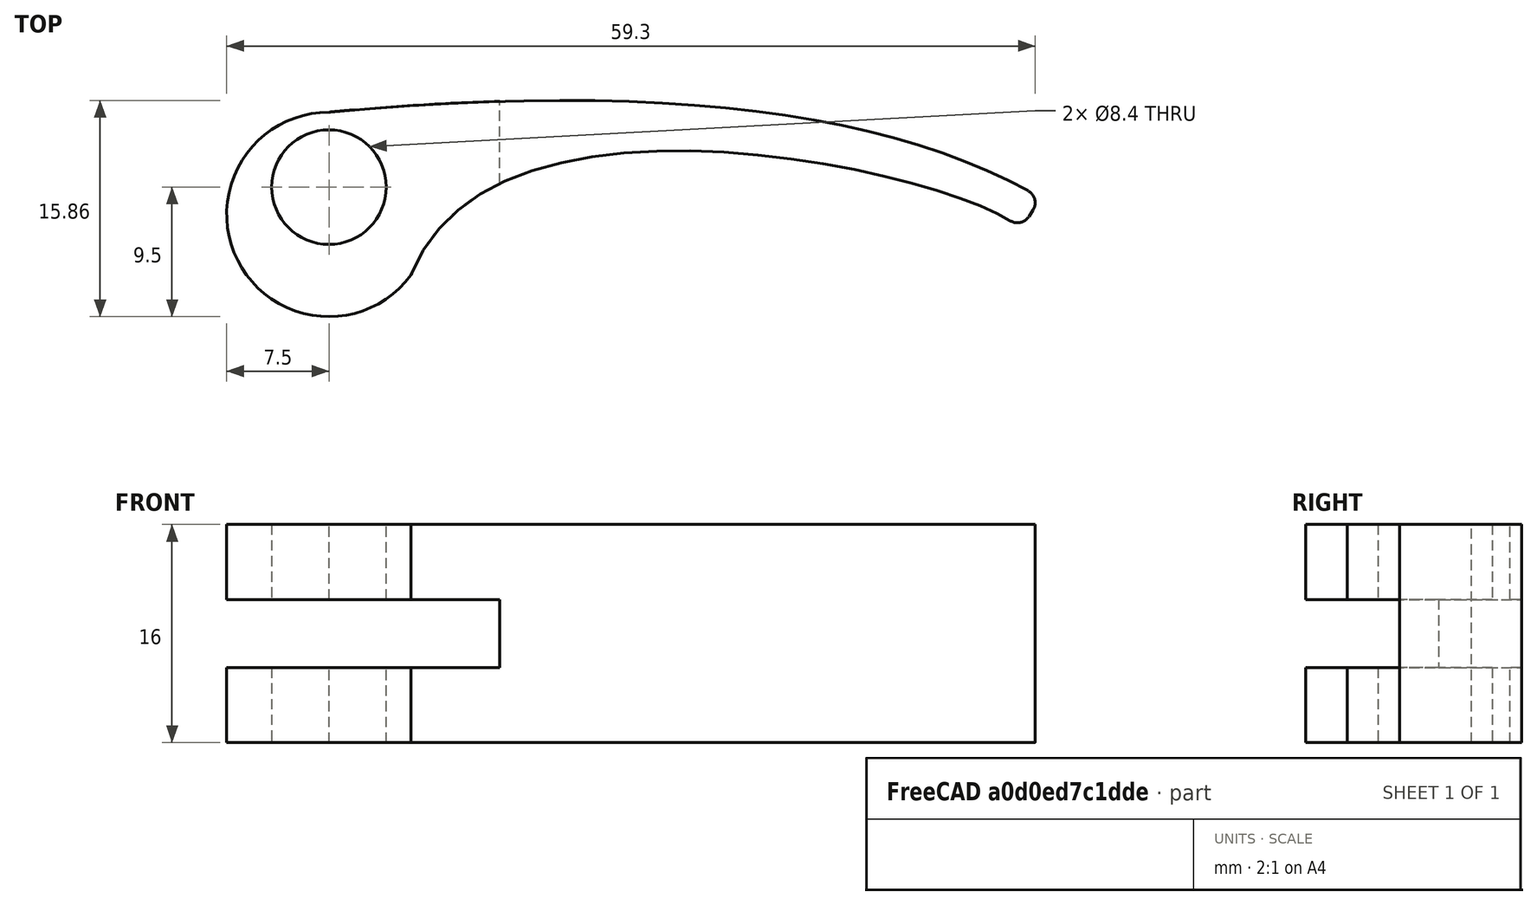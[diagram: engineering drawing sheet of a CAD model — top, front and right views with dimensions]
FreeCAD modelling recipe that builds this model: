
FCSTD DOCUMENT  (FreeCAD 0.18R16131 (Git))
Label: quick_release_handle
License: All rights reserved
LicenseURL: http://en.wikipedia.org/wiki/All_rights_reserved
objects: Sketcher::SketchObject×2, PartDesign::Pad×1, PartDesign::Fillet×1, PartDesign::Pocket×1, PartDesign::Body×1
note: 8 computed .brp shape members not serialized (recipe doc carries the construction recipe); baked Part::Feature solids carry a one-line shape summary decoded from their .brp

FEATURE [Sketcher::SketchObject] Sketch
  MapMode = 5
  Support = -> [XY_Plane]
  sketch-geometry (16):
    g0: Circle CenterX=0 CenterY=0 CenterZ=0 NormalX=0 NormalY=0 NormalZ=1 AngleXU=0 Radius=4.2
    g1: ArcOfCircle CenterX=0 CenterY=-2 CenterZ=0 NormalX=0 NormalY=0 NormalZ=1 AngleXU=0 Radius=7.5 StartAngle=1.5708 EndAngle=5.64644
    g2: Circle [constr] CenterX=0 CenterY=5.5 CenterZ=0 NormalX=0 NormalY=0 NormalZ=1 AngleXU=0 Radius=8
    g3: Circle [constr] CenterX=35.9182 CenterY=8.82437 CenterZ=0 NormalX=0 NormalY=0 NormalZ=1 AngleXU=0 Radius=8
    g4: Circle [constr] CenterX=52.2041 CenterY=-0.7977 CenterZ=0 NormalX=0 NormalY=0 NormalZ=1 AngleXU=0 Radius=7.92
    g5: BSplineCurve PolesCount=3 KnotsCount=2 Degree=2 IsPeriodic=0
    g6: GeomPoint [constr] X=0 Y=5.5 Z=0
    g7: GeomPoint [constr] X=52.2041 Y=-0.7977 Z=0
    g8-g11: Circle [constr] x4 (B-spline internal-alignment scaffolding for g12; pole/knot coordinates omitted)
    g12: BSplineCurve PolesCount=4 KnotsCount=2 Degree=3 IsPeriodic=0
    g13: GeomPoint [constr] X=6.03028 Y=-6.45934 Z=0
    g14: GeomPoint [constr] X=50.756 Y=-3.07354 Z=0
    g15: LineSegment StartX=50.756 StartY=-3.07354 StartZ=0 EndX=52.2041 EndY=-0.7977 EndZ=0
  constraints (15):
    c: Coincident(g0,g-1)
    c: PointOnObject(g1,g-2)
    c: Equal(g2,g3)
    c: InternalAlignment(g2,g5)
    c: InternalAlignment(g3,g5)
    c: InternalAlignment(g4,g5)
    c: InternalAlignment(g6,g5)
    c: InternalAlignment(g7,g5)
    c: Equal(g8,g9)
    c: Equal(g8,g10)
    c: Equal(g8,g11)
    c: InternalAlignment(g8-g11 -> g12) x4
    c: InternalAlignment(g13,g12)
    c: InternalAlignment(g14,g12)
    c: Coincident(g15,g5)
FEATURE [PartDesign::Pad] Pad
  Length = 16
  Length2 = 100
  Midplane = true
  Profile = -> Sketch
  Type = 0
FEATURE [PartDesign::Fillet] Fillet
  Base = -> Pad [Edge5,Edge8]
  BaseFeature = -> Pad
  Radius = 1
FEATURE [Sketcher::SketchObject] Sketch001
  MapMode = 5
  Placement = pos=(0,0,0) rot=(1,0,0;1.5708rad)
  Support = -> [XZ_Plane]
  sketch-geometry (4):
    g0: LineSegment StartX=-16.0826 StartY=2.5 StartZ=0 EndX=12.5355 EndY=2.5 EndZ=0
    g1: LineSegment StartX=12.5355 StartY=2.5 StartZ=0 EndX=12.5355 EndY=-2.5 EndZ=0
    g2: LineSegment StartX=12.5355 StartY=-2.5 StartZ=0 EndX=-16.0826 EndY=-2.5 EndZ=0
    g3: LineSegment StartX=-16.0826 StartY=-2.5 StartZ=0 EndX=-16.0826 EndY=2.5 EndZ=0
  constraints (9):
    c: Coincident(g0,g1)
    c: Coincident(g1,g2)
    c: Coincident(g2,g3)
    c: Coincident(g3,g0)
    c: Horizontal(g0)
    c: Horizontal(g2)
    c: Vertical(g1)
    c: DistanceY(g2,g0) = 5
    c: Symmetric(g2,g0,g-1)
FEATURE [PartDesign::Pocket] Pocket
  BaseFeature = -> Fillet
  Length = 5
  Length2 = 100
  Midplane = true
  Profile = -> Sketch001
  Type = 1
FEATURE [PartDesign::Body] Body
  Group = -> [Sketch,Pad,Fillet,Sketch001,Pocket]
  Origin = -> Origin
  Tip = -> Pocket
